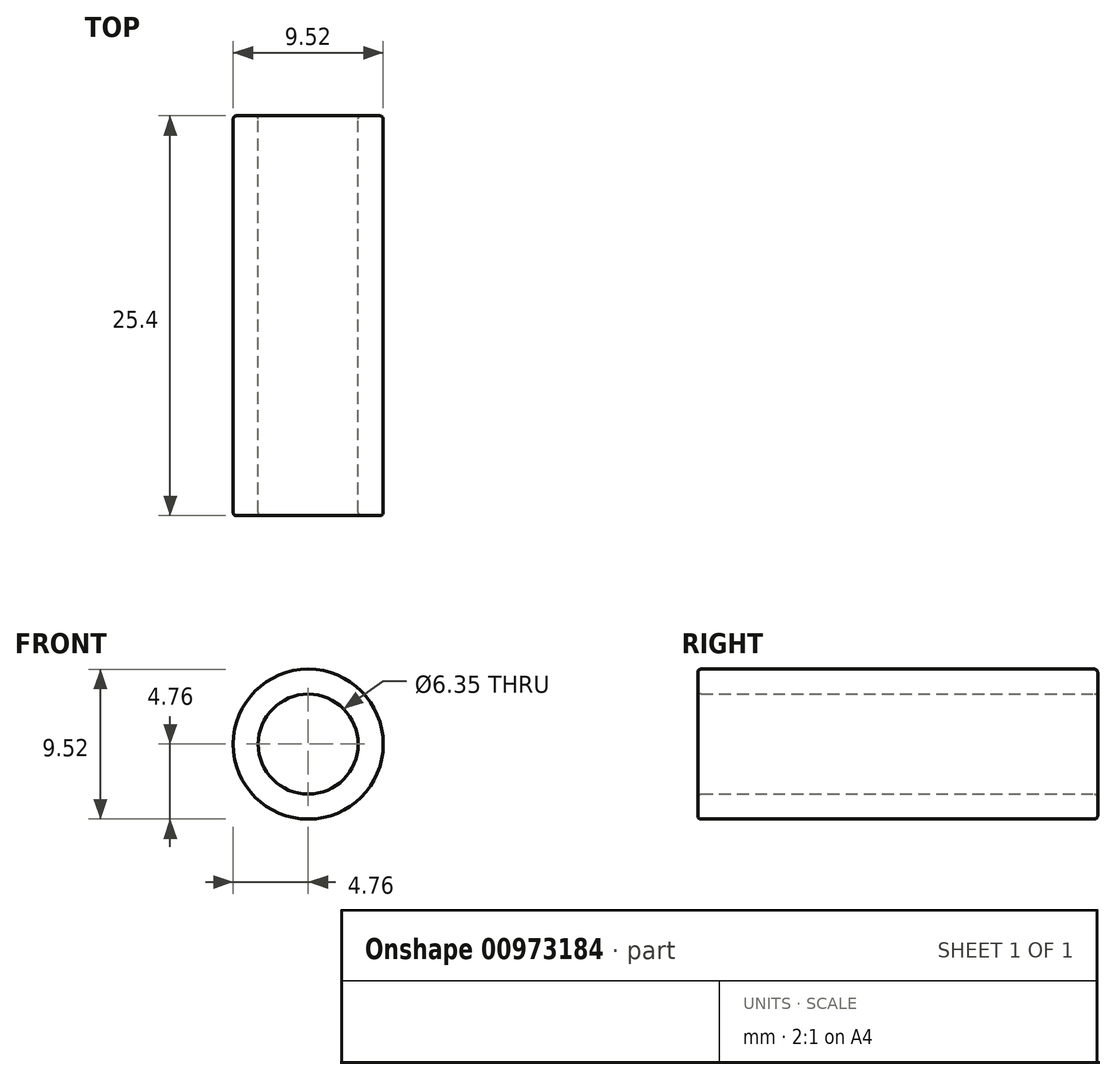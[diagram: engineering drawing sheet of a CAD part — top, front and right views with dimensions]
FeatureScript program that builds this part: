
annotation { "Feature Type Name" : "Feature", "Feature Type Description" : "" }
export const myFeature = defineFeature(function(context is Context, id is Id, definition is map)
    precondition{}
    {
        {
            var Q0;
            Q0=qCreatedBy(makeId("Front.planeOp"),FACE);
            var sketch = newSketch(context, id + "F0", { "sketchPlane" : qUnion([Q0])});
            skCircle(sketch, "E0", {"center": v(0, 0) * mm, "radius": 3.18 * mm});
            skCircle(sketch, "E1", {"center": v(0, 0) * mm, "radius": 4.76 * mm});
            skSolve(sketch);
        }
        {
            var Q0;
            Q0=qSketchRegion(id+"F0",true);
            extrude(context, id + "F1", {"entities" : qUnion([Q0]), "depth" : 25.4 * mm, "offsetDistance" : 25.4 * mm});
        }
        {
            var Q0;
            Q0=makeQuery(id+"F1.opExtrude","CAP_EDGE",EDGE,{"disambiguationData":[OSD([sQuery(id+"F0.wireOp",EDGE,"E0")])],"isStart":false});
            var Q1;
            Q1=makeQuery(id+"F1.opExtrude","CAP_EDGE",EDGE,{"disambiguationData":[OSD([sQuery(id+"F0.wireOp",EDGE,"E1")])],"isStart":false});
            var Q2;
            Q2=makeQuery(id+"F1.opExtrude","CAP_EDGE",EDGE,{"disambiguationData":[OSD([sQuery(id+"F0.wireOp",EDGE,"E1")])],"isStart":true});
            var Q3;
            Q3=makeQuery(id+"F1.opExtrude","CAP_EDGE",EDGE,{"disambiguationData":[OSD([sQuery(id+"F0.wireOp",EDGE,"E0")])],"isStart":true});
            fillet(context, id + "F2", {"entities" : qUnion([Q0, Q1, Q2, Q3]), "radius" : 0.2 * mm, "tangentPropagation" : true, "allowEdgeOverflow" : false});
        }
    });
